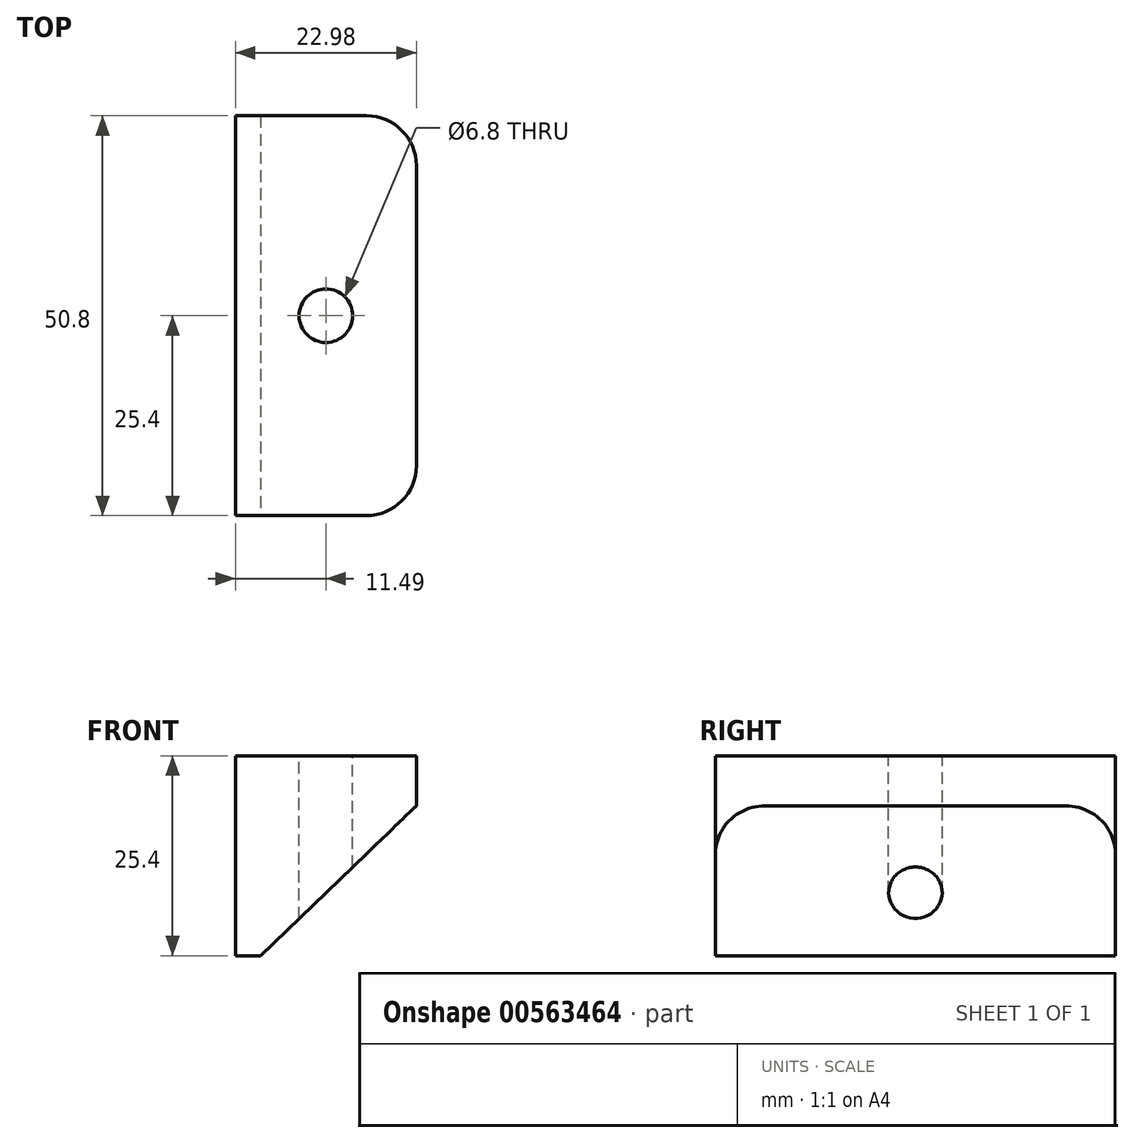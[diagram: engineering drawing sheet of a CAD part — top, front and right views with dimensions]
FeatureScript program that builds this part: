
annotation { "Feature Type Name" : "Feature", "Feature Type Description" : "" }
export const myFeature = defineFeature(function(context is Context, id is Id, definition is map)
    precondition{}
    {
        {
            var Q0;
            Q0=qCreatedBy(makeId("Front.planeOp"),FACE);
            var sketch = newSketch(context, id + "F0", { "sketchPlane" : qUnion([Q0])});
            skLineSegment(sketch, "E0.bottom", {"start": v(-11.5, 12.7) * mm, "end": v(11.5, 12.7) * mm});
            skLineSegment(sketch, "E0.top", {"start": v(-11.5, -12.7) * mm, "end": v(11.5, -12.7) * mm});
            skLineSegment(sketch, "E0.left", {"start": v(-11.5, 12.7) * mm, "end": v(-11.5, -12.7) * mm});
            skLineSegment(sketch, "E0.right", {"start": v(11.5, 12.7) * mm, "end": v(11.5, -12.7) * mm});
            skPoint(sketch, "E0.middle", {"position": v(0, 0) * mm});
            skSolve(sketch);
        }
        {
            var Q0;
            Q0=makeQuery(id+"F0.imprint","IMPRINT",FACE,{"disambiguationData":[TD([[makeQuery(id+"F0.imprint","IMPRINT",EDGE,{"derivedFrom":sQuery(id+"F0.wireOp",EDGE,"E0.bottom")}),-1.0]])]});
            extrude(context, id + "F1", {"entities" : qUnion([Q0]), "endBound" : BoundingType.SYMMETRIC, "depth" : 50.8 * mm, "offsetDistance" : 25.4 * mm});
        }
        {
            var Q0;
            Q0=makeQuery(id+"F1.opExtrude","CAP_EDGE",EDGE,{"disambiguationData":[OSD([sQuery(id+"F0.wireOp",EDGE,"E0.right")])],"isStart":true});
            var Q1;
            Q1=makeQuery(id+"F1.opExtrude","CAP_EDGE",EDGE,{"disambiguationData":[OSD([sQuery(id+"F0.wireOp",EDGE,"E0.right")])],"isStart":false});
            fillet(context, id + "F2", {"entities" : qUnion([Q0, Q1]), "radius" : 6.35 * mm, "tangentPropagation" : true, "allowEdgeOverflow" : false});
        }
        {
            var Q0;
            Q0=makeQuery(id+"F1.opExtrude","SWEPT_FACE",FACE,{"disambiguationData":[OSD([sQuery(id+"F0.wireOp",EDGE,"E0.bottom")])]});
            var sketch = newSketch(context, id + "F3", { "sketchPlane" : qUnion([Q0])});
            skPoint(sketch, "E1", {"position": v(0, 0) * mm});
            skSolve(sketch);
        }
        {
            var Q0;
            Q0=sQuery(id+"F3.wireOp",VERTEX,"E1");
            var Q1;
            Q1=makeQuery(id+"F1.opExtrude","SWEPT_BODY",BODY,{"disambiguationData":[OSD([sQuery(id+"F0.wireOp",EDGE,"E0.bottom"),sQuery(id+"F0.wireOp",EDGE,"E0.top"),sQuery(id+"F0.wireOp",EDGE,"E0.left"),sQuery(id+"F0.wireOp",EDGE,"E0.right")])]});
            hole(context, id + "F4", {"style" : HoleStyle.SIMPLE, "endStyle" : HoleEndStyle.THROUGH, "standardTappedOrClearance" : lookupTablePath({ "standard" : "ISO", "engagement" : "75%", "pitch" : "1.25 mm", "size" : "M8", "type" : "Tapped" }), "standardBlindInLast" : lookupTablePath({ "standard" : "ISO", "engagement" : "75%", "pitch" : "1.25 mm", "size" : "M8", "type" : "Tapped" }), "holeDiameter" : 6.8 * mm, "showTappedDepth" : true, "isTappedThrough" : true, "tappedDepth" : 34.3 * mm, "tapClearance" : 3, "locations" : qUnion([Q0]), "scope" : qUnion([Q1]), "majorDiameter" : 8 * mm});
        }
        {
            var Q0;
            Q0=makeQuery(id+"F1.opExtrude","SWEPT_EDGE",EDGE,{"disambiguationData":[OSD([sQuery(id+"F0.wireOp",EDGE,"E0.top"),sQuery(id+"F0.wireOp",EDGE,"E0.right")])]});
            chamfer(context, id + "F5", {"entities" : qUnion([Q0]), "chamferType" : ChamferType.TWO_OFFSETS, "width1" : 19.05 * mm, "oppositeDirection" : false, "width2" : 19.8 * mm});
        }
    });
